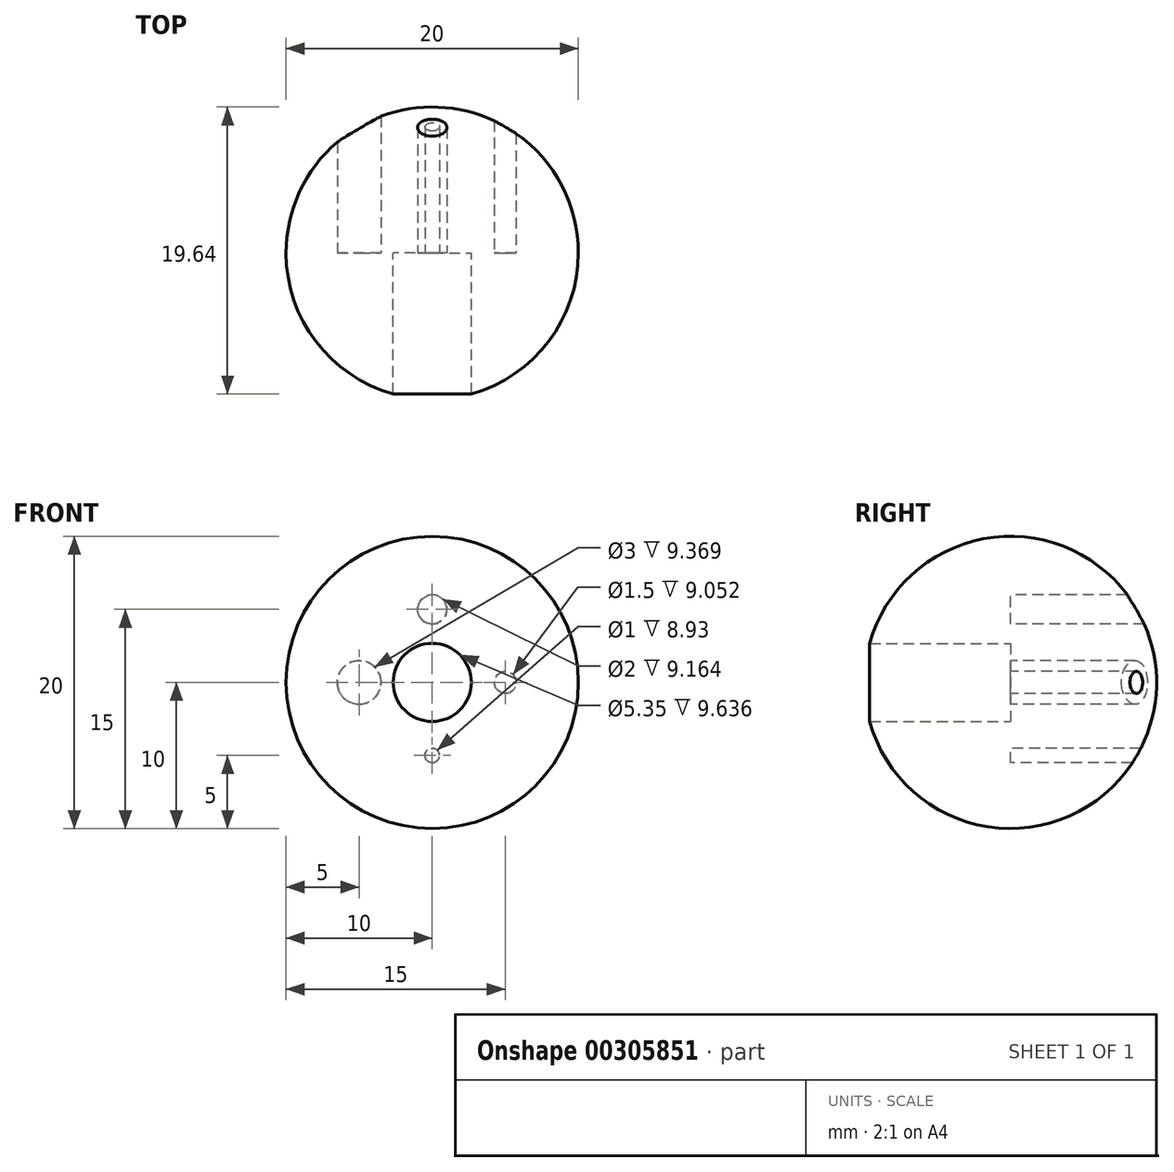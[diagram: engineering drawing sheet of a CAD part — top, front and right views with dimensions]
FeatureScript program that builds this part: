
annotation { "Feature Type Name" : "Feature", "Feature Type Description" : "" }
export const myFeature = defineFeature(function(context is Context, id is Id, definition is map)
    precondition{}
    {
        {
            var Q0;
            Q0=qCreatedBy(makeId("Front.planeOp"),FACE);
            var sketch = newSketch(context, id + "F0", { "sketchPlane" : qUnion([Q0])});
            skPoint(sketch, "E0.endSnap0", {"position": v(0, -12.5) * mm});
            skArc(sketch, "E1", {"start": v(-10, 0) * mm, "mid": v(0, -10) * mm, "end": v(10, 0) * mm});
            skLineSegment(sketch, "E2", {"start": v(-10, 0) * mm, "end": v(10, 0) * mm});
            skSolve(sketch);
        }
        {
            var Q0;
            Q0=qCreatedBy(makeId("Front.planeOp"),FACE);
            cPlane(context, id + "F1", {"entities" : qUnion([Q0]), "cplaneType" : CPlaneType.OFFSET, "offset" : 5 * mm, "oppositeDirection" : true, "width" : 150 * mm, "height" : 150 * mm});
        }
        {
            var Q0;
            Q0=makeQuery(id+"F0.imprint","IMPRINT",FACE,{"disambiguationData":[TD([[makeQuery(id+"F0.imprint","IMPRINT",EDGE,{"derivedFrom":sQuery(id+"F0.wireOp",EDGE,"E1")}),1.0]])]});
            var Q1;
            Q1=sQuery(id+"F0.wireOp",EDGE,"E2");
            revolve(context, id + "F2", {"entities" : qUnion([Q0]), "axis" : qUnion([Q1]), "revolveType" : RevolveType.FULL});
        }
        {
            var Q0;
            Q0=qCreatedBy(id+"F1.planeOp",FACE);
            var sketch = newSketch(context, id + "F3", { "sketchPlane" : qUnion([Q0])});
            skCircle(sketch, "E3", {"center": v(0, 0) * mm, "radius": 5 * mm, "construction": true});
            skCircle(sketch, "E4", {"center": v(0, 5) * mm, "radius": 1 * mm});
            skCircle(sketch, "E5", {"center": v(0, -5) * mm, "radius": 0.5 * mm});
            skCircle(sketch, "E6", {"center": v(5, 0) * mm, "radius": 0.75 * mm});
            skCircle(sketch, "E7", {"center": v(-5, 0) * mm, "radius": 1.5 * mm});
            skSolve(sketch);
        }
        {
            var Q0;
            Q0 = qSketchRegion(id + "F3", true);
            extrude(context, id + "F4", {"entities" : qUnion([Q0]), "operationType" : NewBodyOperationType.REMOVE, "endBound" : BoundingType.SYMMETRIC, "oppositeDirection" : true, "depth" : 10 * mm});
        }
        {
            var Q0;
            Q0=qCreatedBy(makeId("Front.planeOp"),FACE);
            var sketch = newSketch(context, id + "F5", { "sketchPlane" : qUnion([Q0])});
            skCircle(sketch, "E8", {"center": v(0, 0) * mm, "radius": 2.67 * mm});
            skSolve(sketch);
        }
        {
            var Q0;
            Q0 = qSketchRegion(id + "F5", true);
            var Q1;
            Q1=sQuery(id+"F5.wireOp",EDGE,"E8");
            extrude(context, id + "F6", {"entities" : qUnion([Q0]), "operationType" : NewBodyOperationType.REMOVE, "surfaceEntities" : qUnion([Q1]), "depth" : 50 * mm});
        }
    });
